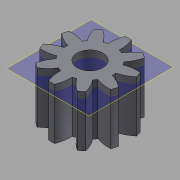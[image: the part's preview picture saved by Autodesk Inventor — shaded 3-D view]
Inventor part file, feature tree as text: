
AUTODESK INVENTOR PART (.ipt)
format: ipt  version: 2015 (Build 190159000, 159)  size: 167,936 bytes
history: native  units: in
note: dims shown in document units (in); Inventor stores cm internally (conversion verified against a paired STEP export)
features: other x13, sketch x3, plane x2
ambient origin geometry x8: Origin, YZ Plane, XZ Plane, XY Plane, X Axis, Y Axis, Z Axis, Center Point
bodies: Solid1 (feature_tree)
feature tree (18):
  other  "Spur Gear18_MIR2.ipt"
  other  "Solid1::Spur Gear18_MIR2.ipt"
  other  "TaggingFeature1"
  sketch  "Sketch1"  dims[d0=0.3937in]
  sketch  "Sketch2"  dims[d16=0.4528in d17=0.0in d41=0.0in d43=0.4528in d46=0.4528in d47=0.0in d48=0.0in]
  sketch  "Sketch3"
  plane  "XZ Plane_1"
  plane  "Work Plane2"
  other  "Z Axis_1"
  other  "Srf1"
  other  "Srf1::Derived"
  other  "Distance iMate"
  other  "Align iMate"
  other  "Mesh iMate"
  other  "Axis iMate"
  other  "Position iMate"
  other  "Mesh iMate2"
  other  "Start plane iMate"
